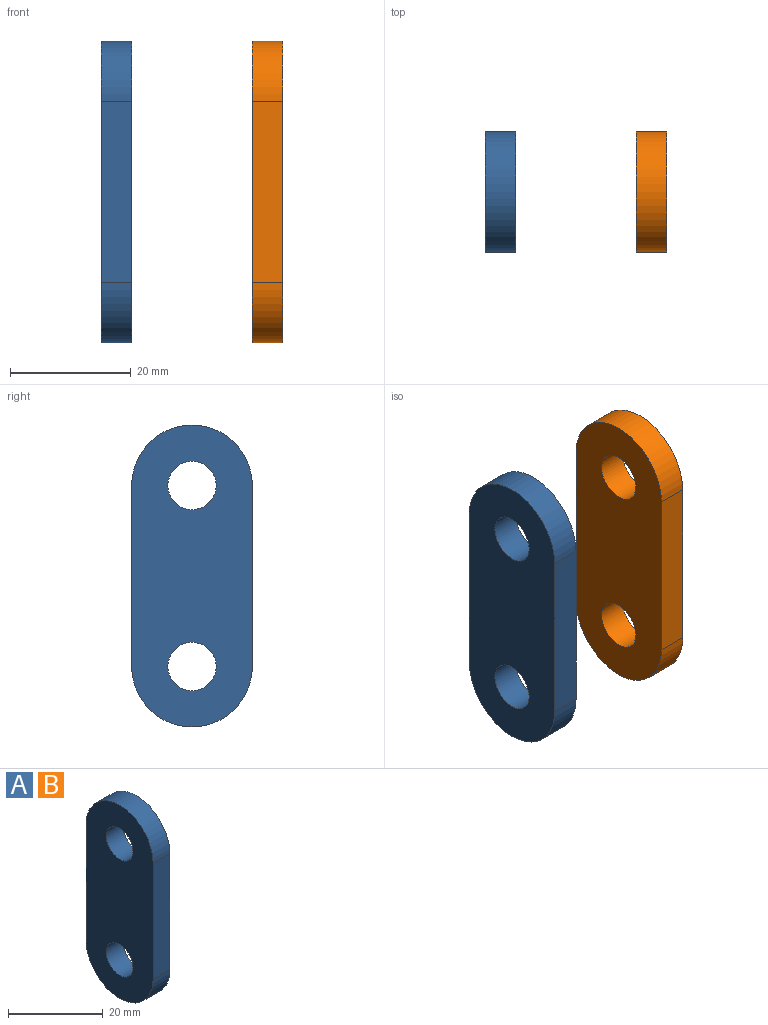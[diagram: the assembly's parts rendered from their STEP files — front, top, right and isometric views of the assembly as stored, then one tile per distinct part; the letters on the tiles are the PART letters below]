
ASSEMBLY  parts=2 mates=1
PART A: 8 faces, bbox 5x20x50 mm
  f0: cylinder r=10mm len=20mm, axis (-1,0,0), area 157.1mm2, adj f1,f5,f6,f7
  f1: plane 30x5mm, normal (0,-1,0), area 150mm2, adj f0,f2,f6,f7
  f2: cylinder r=10mm len=20mm, axis (-1,0,0), area 157.1mm2, adj f1,f5,f6,f7
  f3: cylinder r=4mm len=8mm, axis (-1,0,0), area 125.7mm2, adj f6,f7
  f4: cylinder r=4mm len=8mm, axis (-1,0,0), area 125.7mm2, adj f6,f7
  f5: plane 30x5mm, normal (0,1,0), area 150mm2, adj f0,f2,f6,f7
  f6: plane 50x20mm, normal (1,0,0), area 813.6mm2, adj f0,f1,f2,f3,f4,f5
  f7: plane 50x20mm, normal (-1,0,0), area 813.6mm2, adj f0,f1,f2,f3,f4,f5
PART B: same geometry as A
PLACE A t=(-12.5,0,0)mm
PLACE B t=(12.5,0,0)mm
MATE fastened A.f2 <-> B.f2  axis (-1,0,0) through (-10,0,0)mm
